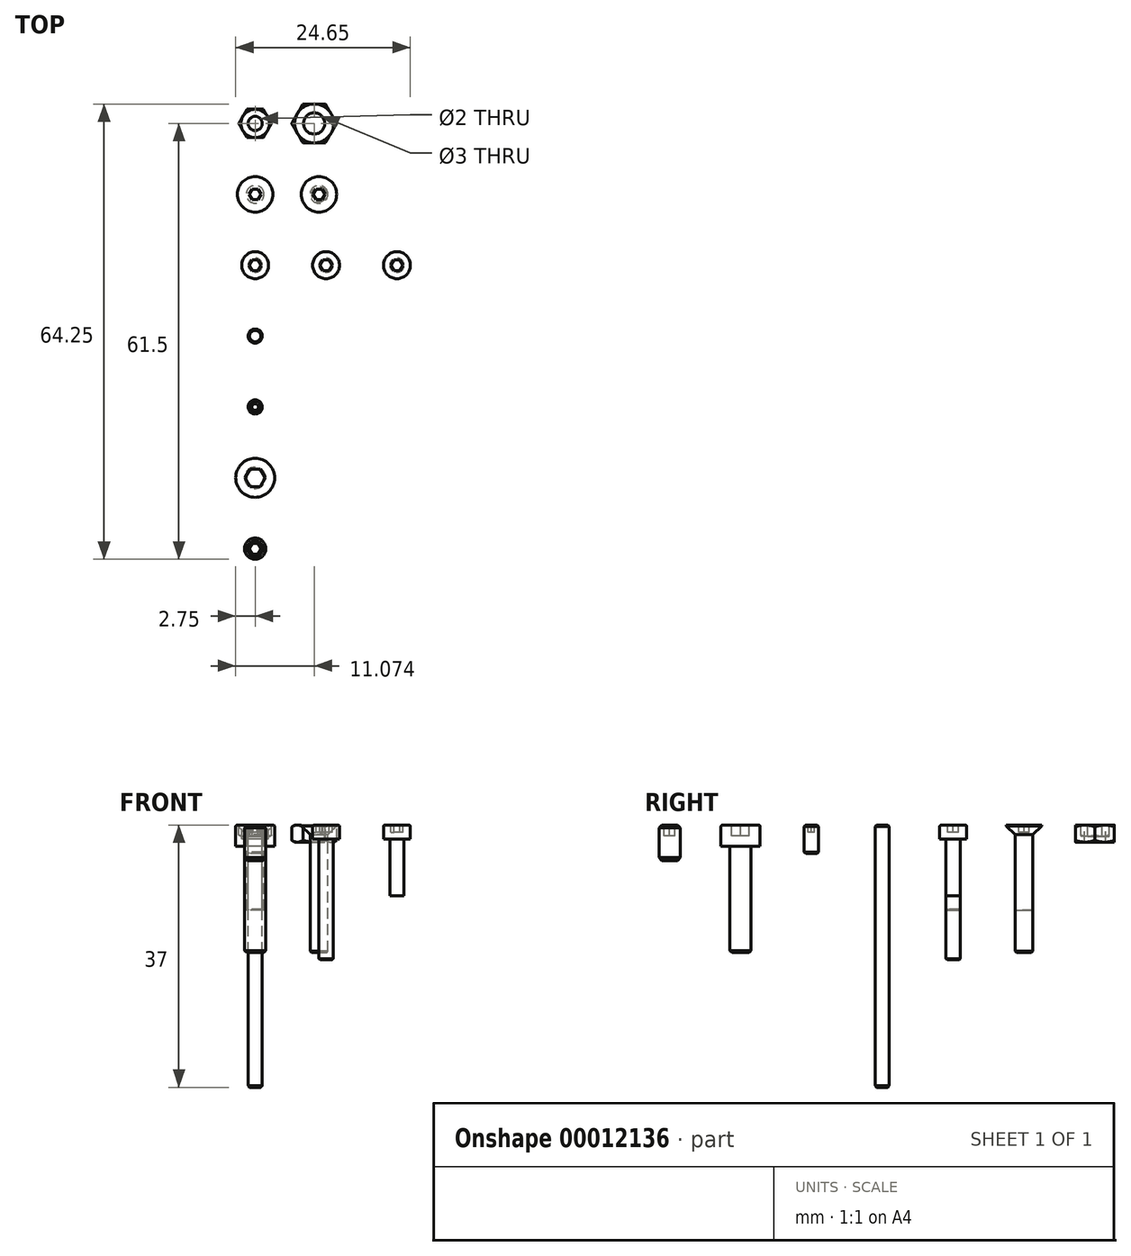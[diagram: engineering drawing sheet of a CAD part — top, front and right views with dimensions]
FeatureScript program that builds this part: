
annotation { "Feature Type Name" : "Feature", "Feature Type Description" : "" }
export const myFeature = defineFeature(function(context is Context, id is Id, definition is map)
    precondition{}
    {
        {
            var Q0;
            Q0=qCreatedBy(makeId("Top.planeOp"),FACE);
            var sketch = newSketch(context, id + "F0", { "sketchPlane" : qUnion([Q0])});
            skCircle(sketch, "E0.cCircle", {"center": v(0, 0) * mm, "radius": 2 * mm, "construction": true});
            skLineSegment(sketch, "E0.0", {"start": v(1.15, -2) * mm, "end": v(-1.15, -2) * mm});
            skLineSegment(sketch, "E0.1", {"start": v(-1.15, -2) * mm, "end": v(-2.3, 0) * mm});
            skLineSegment(sketch, "E0.2", {"start": v(-2.3, 0) * mm, "end": v(-1.15, 2) * mm});
            skLineSegment(sketch, "E0.3", {"start": v(-1.15, 2) * mm, "end": v(1.15, 2) * mm});
            skLineSegment(sketch, "E0.4", {"start": v(1.15, 2) * mm, "end": v(2.3, 0) * mm});
            skLineSegment(sketch, "E0.5", {"start": v(2.3, 0) * mm, "end": v(1.15, -2) * mm});
            skPoint(sketch, "E0.0.midPoint", {"position": v(0, -2) * mm});
            skCircle(sketch, "E1", {"center": v(0, 0) * mm, "radius": 1 * mm});
            skCircle(sketch, "E2", {"center": v(0, 0) * mm, "radius": 2 * mm});
            skSolve(sketch);
        }
        {
            var Q0;
            {var subQ1=sQuery(id+"F0.wireOp",EDGE,"E0.3");var subQ3=sQuery(id+"F0.wireOp",EDGE,"E0.2");var subQ5=makeQuery(id+"F0.imprint","INTERSECT",VERTEX,{"derivedFrom":[subQ3,subQ1]});Q0=makeQuery(id+"F0.imprint","IMPRINT",FACE,{"disambiguationData":[TD([[makeQuery(id+"F0.imprint","IMPRINT",EDGE,{"disambiguationData":[TD([[subQ5,1.0]])],"derivedFrom":subQ3}),-1.0]])]});}
            var Q1;
            {var subQ1=sQuery(id+"F0.wireOp",EDGE,"E0.2");var subQ3=sQuery(id+"F0.wireOp",EDGE,"E0.1");var subQ5=makeQuery(id+"F0.imprint","INTERSECT",VERTEX,{"derivedFrom":[subQ3,subQ1]});Q1=makeQuery(id+"F0.imprint","IMPRINT",FACE,{"disambiguationData":[TD([[makeQuery(id+"F0.imprint","IMPRINT",EDGE,{"disambiguationData":[TD([[subQ5,1.0]])],"derivedFrom":subQ3}),-1.0]])]});}
            var Q2;
            Q2=makeQuery(id+"F0.imprint","IMPRINT",FACE,{"disambiguationData":[TD([[makeQuery(id+"F0.imprint","IMPRINT",EDGE,{"derivedFrom":sQuery(id+"F0.wireOp",EDGE,"E1")}),-1.0]])]});
            var Q3;
            {var subQ1=sQuery(id+"F0.wireOp",EDGE,"E0.4");var subQ3=sQuery(id+"F0.wireOp",EDGE,"E0.3");var subQ5=makeQuery(id+"F0.imprint","INTERSECT",VERTEX,{"derivedFrom":[subQ3,subQ1]});Q3=makeQuery(id+"F0.imprint","IMPRINT",FACE,{"disambiguationData":[TD([[makeQuery(id+"F0.imprint","IMPRINT",EDGE,{"disambiguationData":[TD([[subQ5,1.0]])],"derivedFrom":subQ3}),-1.0]])]});}
            var Q4;
            {var subQ1=sQuery(id+"F0.wireOp",EDGE,"E0.5");var subQ3=sQuery(id+"F0.wireOp",EDGE,"E0.4");var subQ5=makeQuery(id+"F0.imprint","INTERSECT",VERTEX,{"derivedFrom":[subQ3,subQ1]});Q4=makeQuery(id+"F0.imprint","IMPRINT",FACE,{"disambiguationData":[TD([[makeQuery(id+"F0.imprint","IMPRINT",EDGE,{"disambiguationData":[TD([[subQ5,1.0]])],"derivedFrom":subQ3}),-1.0]])]});}
            var Q5;
            {var subQ1=sQuery(id+"F0.wireOp",EDGE,"E0.5");var subQ3=sQuery(id+"F0.wireOp",EDGE,"E0.0");var subQ5=makeQuery(id+"F0.imprint","INTERSECT",VERTEX,{"derivedFrom":[subQ3,subQ1]});Q5=makeQuery(id+"F0.imprint","IMPRINT",FACE,{"disambiguationData":[TD([[makeQuery(id+"F0.imprint","IMPRINT",EDGE,{"disambiguationData":[TD([[subQ5,-1.0]])],"derivedFrom":subQ3}),-1.0]])]});}
            var Q6;
            {var subQ1=sQuery(id+"F0.wireOp",EDGE,"E0.1");var subQ3=sQuery(id+"F0.wireOp",EDGE,"E0.0");var subQ5=makeQuery(id+"F0.imprint","INTERSECT",VERTEX,{"derivedFrom":[subQ3,subQ1]});Q6=makeQuery(id+"F0.imprint","IMPRINT",FACE,{"disambiguationData":[TD([[makeQuery(id+"F0.imprint","IMPRINT",EDGE,{"disambiguationData":[TD([[subQ5,1.0]])],"derivedFrom":subQ3}),-1.0]])]});}
            extrude(context, id + "F1", {"entities" : qUnion([Q0, Q1, Q2, Q3, Q4, Q5, Q6]), "oppositeDirection" : true, "depth" : 1.6 * mm});
        }
        {
            var Q0;
            Q0=qCreatedBy(makeId("Front.planeOp"),FACE);
            var sketch = newSketch(context, id + "F2", { "sketchPlane" : qUnion([Q0])});
            skLineSegment(sketch, "E3.0", {"start": v(-2, 0) * mm, "end": v(2, 0) * mm});
            skLineSegment(sketch, "E3.1", {"start": v(2.3, -1.6) * mm, "end": v(2.3, 0) * mm});
            skLineSegment(sketch, "E3.2", {"start": v(-2.3, -1.6) * mm, "end": v(-2.3, 0) * mm});
            skLineSegment(sketch, "E4", {"start": v(2, 0) * mm, "end": v(2.3, -0.18) * mm});
            skLineSegment(sketch, "E5", {"start": v(2, 0) * mm, "end": v(2.3, 0) * mm});
            skLineSegment(sketch, "E6", {"start": v(0, 0) * mm, "end": v(0, -1.88) * mm, "construction": true});
            skLineSegment(sketch, "E7", {"start": v(-2.3, -0.8) * mm, "end": v(0, -0.8) * mm, "construction": true});
            skLineSegment(sketch, "E8.0.MirrorCS", {"start": v(2, -1.6) * mm, "end": v(2.3, -1.6) * mm});
            skLineSegment(sketch, "E9.0.MirrorCS", {"start": v(2.3, 0) * mm, "end": v(2.3, -1.6) * mm});
            skLineSegment(sketch, "E10.0.MirrorCS", {"start": v(2, -1.6) * mm, "end": v(2.3, -1.42) * mm});
            skSolve(sketch);
        }
        {
            var Q0;
            {var subQ2=sQuery(id+"F2.wireOp",EDGE,"E4");Q0=makeQuery(id+"F2.imprint","IMPRINT",FACE,{"disambiguationData":[TD([[makeQuery(id+"F2.imprint","IMPRINT",EDGE,{"derivedFrom":subQ2}),1.0]])]});}
            var Q1;
            {var subQ2=sQuery(id+"F2.wireOp",EDGE,"E8.0.MirrorCS");Q1=makeQuery(id+"F2.imprint","IMPRINT",FACE,{"disambiguationData":[TD([[makeQuery(id+"F2.imprint","IMPRINT",EDGE,{"derivedFrom":subQ2}),1.0]])]});}
            var Q2;
            Q2=sQuery(id+"F2.wireOp",EDGE,"E6");
            revolve(context, id + "F3", {"operationType" : NewBodyOperationType.REMOVE, "entities" : qUnion([Q0, Q1]), "axis" : qUnion([Q2]), "revolveType" : RevolveType.FULL, "oppositeDirection" : true});
        }
        {
            var Q0;
            Q0=qCreatedBy(makeId("Top.planeOp"),FACE);
            var sketch = newSketch(context, id + "F4", { "sketchPlane" : qUnion([Q0])});
            skCircle(sketch, "E11.cCircle", {"center": v(8.32, 0) * mm, "radius": 2.75 * mm, "construction": true});
            skLineSegment(sketch, "E11.0", {"start": v(9.91, -2.75) * mm, "end": v(6.74, -2.75) * mm});
            skLineSegment(sketch, "E11.1", {"start": v(6.74, -2.75) * mm, "end": v(5.15, 0) * mm});
            skLineSegment(sketch, "E11.2", {"start": v(5.15, 0) * mm, "end": v(6.74, 2.75) * mm});
            skLineSegment(sketch, "E11.3", {"start": v(6.74, 2.75) * mm, "end": v(9.91, 2.75) * mm});
            skLineSegment(sketch, "E11.4", {"start": v(9.91, 2.75) * mm, "end": v(11.5, 0) * mm});
            skLineSegment(sketch, "E11.5", {"start": v(11.5, 0) * mm, "end": v(9.91, -2.75) * mm});
            skPoint(sketch, "E11.0.midPoint", {"position": v(8.32, -2.75) * mm});
            skCircle(sketch, "E12", {"center": v(8.32, 0) * mm, "radius": 1.5 * mm});
            skSolve(sketch);
        }
        {
            var Q0;
            Q0=makeQuery(id+"F4.imprint","IMPRINT",FACE,{"disambiguationData":[TD([[makeQuery(id+"F4.imprint","IMPRINT",EDGE,{"derivedFrom":sQuery(id+"F4.wireOp",EDGE,"E11.0")}),-1.0]])]});
            extrude(context, id + "F5", {"entities" : qUnion([Q0]), "oppositeDirection" : true, "depth" : 2.4 * mm});
        }
        {
            var Q0;
            Q0=qCreatedBy(makeId("Front.planeOp"),FACE);
            var sketch = newSketch(context, id + "F6", { "sketchPlane" : qUnion([Q0])});
            skLineSegment(sketch, "E13.0", {"start": v(5.57, 0) * mm, "end": v(11.07, 0) * mm});
            skLineSegment(sketch, "E13.1", {"start": v(5.15, -2.4) * mm, "end": v(5.15, 0) * mm});
            skLineSegment(sketch, "E13.2", {"start": v(11.5, -2.4) * mm, "end": v(11.5, 0) * mm});
            skLineSegment(sketch, "E14", {"start": v(5.57, 0) * mm, "end": v(5.15, -0.25) * mm});
            skLineSegment(sketch, "E15", {"start": v(5.57, 0) * mm, "end": v(5.15, 0) * mm});
            skLineSegment(sketch, "E16", {"start": v(8.32, 0) * mm, "end": v(8.32, -2.47) * mm, "construction": true});
            skLineSegment(sketch, "E17", {"start": v(11.5, -1.2) * mm, "end": v(8.32, -1.2) * mm, "construction": true});
            skLineSegment(sketch, "E18.0.MirrorCS", {"start": v(5.57, -2.4) * mm, "end": v(5.15, -2.15) * mm});
            skLineSegment(sketch, "E19.0.MirrorCS", {"start": v(5.15, 0) * mm, "end": v(5.15, -2.4) * mm});
            skLineSegment(sketch, "E20.0.MirrorCS", {"start": v(5.57, -2.4) * mm, "end": v(5.15, -2.4) * mm});
            skSolve(sketch);
        }
        {
            var Q0;
            {var subQ2=sQuery(id+"F6.wireOp",EDGE,"E14");Q0=makeQuery(id+"F6.imprint","IMPRINT",FACE,{"disambiguationData":[TD([[makeQuery(id+"F6.imprint","IMPRINT",EDGE,{"derivedFrom":subQ2}),-1.0]])]});}
            var Q1;
            {var subQ2=sQuery(id+"F6.wireOp",EDGE,"E18.0.MirrorCS");Q1=makeQuery(id+"F6.imprint","IMPRINT",FACE,{"disambiguationData":[TD([[makeQuery(id+"F6.imprint","IMPRINT",EDGE,{"derivedFrom":subQ2}),1.0]])]});}
            var Q2;
            Q2=sQuery(id+"F6.wireOp",EDGE,"E16");
            revolve(context, id + "F7", {"operationType" : NewBodyOperationType.REMOVE, "entities" : qUnion([Q0, Q1]), "axis" : qUnion([Q2]), "revolveType" : RevolveType.FULL, "oppositeDirection" : true});
        }
        {
            var Q0;
            Q0=qCreatedBy(makeId("Top.planeOp"),FACE);
            var sketch = newSketch(context, id + "F8", { "sketchPlane" : qUnion([Q0])});
            skCircle(sketch, "E21", {"center": v(17, 0) * mm, "radius": 2.5 * mm});
            skCircle(sketch, "E22", {"center": v(17, 0) * mm, "radius": 1.25 * mm});
            skCircle(sketch, "E23.cCircle", {"center": v(17, 0) * mm, "radius": 0.75 * mm, "construction": true});
            skLineSegment(sketch, "E23.0", {"start": v(17.43, -0.75) * mm, "end": v(16.57, -0.75) * mm});
            skLineSegment(sketch, "E23.1", {"start": v(16.57, -0.75) * mm, "end": v(16.13, 0) * mm});
            skLineSegment(sketch, "E23.2", {"start": v(16.13, 0) * mm, "end": v(16.57, 0.75) * mm});
            skLineSegment(sketch, "E23.3", {"start": v(16.57, 0.75) * mm, "end": v(17.43, 0.75) * mm});
            skLineSegment(sketch, "E23.4", {"start": v(17.43, 0.75) * mm, "end": v(17.87, 0) * mm});
            skLineSegment(sketch, "E23.5", {"start": v(17.87, 0) * mm, "end": v(17.43, -0.75) * mm});
            skPoint(sketch, "E23.0.midPoint", {"position": v(17, -0.75) * mm});
            skSolve(sketch);
        }
        {
            var Q0;
            Q0=makeQuery(id+"F8.imprint","IMPRINT",FACE,{"disambiguationData":[TD([[makeQuery(id+"F8.imprint","IMPRINT",EDGE,{"derivedFrom":sQuery(id+"F8.wireOp",EDGE,"E22")}),1.0]])]});
            var Q1;
            Q1=makeQuery(id+"F8.imprint","IMPRINT",FACE,{"disambiguationData":[TD([[makeQuery(id+"F8.imprint","IMPRINT",EDGE,{"derivedFrom":sQuery(id+"F8.wireOp",EDGE,"E23.0")}),-1.0]])]});
            extrude(context, id + "F9", {"entities" : qUnion([Q0, Q1]), "oppositeDirection" : true, "depth" : 15 * mm});
        }
        {
            var Q0;
            Q0=makeQuery(id+"F8.imprint","IMPRINT",FACE,{"disambiguationData":[TD([[makeQuery(id+"F8.imprint","IMPRINT",EDGE,{"derivedFrom":sQuery(id+"F8.wireOp",EDGE,"E21")}),1.0]])]});
            extrude(context, id + "F10", {"entities" : qUnion([Q0]), "operationType" : NewBodyOperationType.ADD, "oppositeDirection" : true, "depth" : 1.5 * mm});
        }
        {
            var Q0;
            Q0=makeQuery(id+"F10.opExtrude","CAP_EDGE",EDGE,{"disambiguationData":[OSD([sQuery(id+"F8.wireOp",EDGE,"E21")])],"isStart":false});
            chamfer(context, id + "F11", {"entities" : qUnion([Q0]), "width" : 1.4 * mm, "tangentPropagation" : true});
        }
        {
            var Q0;
            Q0=makeQuery(id+"F8.imprint","IMPRINT",FACE,{"disambiguationData":[TD([[makeQuery(id+"F8.imprint","IMPRINT",EDGE,{"derivedFrom":sQuery(id+"F8.wireOp",EDGE,"E23.0")}),-1.0]])]});
            extrude(context, id + "F12", {"entities" : qUnion([Q0]), "operationType" : NewBodyOperationType.REMOVE, "oppositeDirection" : true, "depth" : 1 * mm});
        }
        {
            var Q0;
            Q0=makeQuery(id+"F9.opExtrude","SWEPT_BODY",BODY,{"disambiguationData":[OSD([sQuery(id+"F8.wireOp",EDGE,"E22")])]});
            transform(context, id + "F13", {"entities" : qUnion([Q0]), "transformType" : TransformType.TRANSLATION_3D, "dx" : 10 * mm, "dy" : 0 * mm, "dz" : 0 * mm, "makeCopy" : true});
        }
        {
            var Q0;
            Q0=makeQuery(id+"F13.opPattern","COPY",FACE,{"derivedFrom":makeQuery(id+"F9.opExtrude","CAP_FACE",FACE,{"disambiguationData":[OSD([sQuery(id+"F8.wireOp",EDGE,"E22")])],"isStart":false}),"instanceName":"1"});
            extrude(context, id + "F14", {"entities" : qUnion([Q0]), "operationType" : NewBodyOperationType.ADD, "depth" : 3 * mm});
        }
        {
            var Q0;
            Q0=makeQuery(id+"F9.opExtrude","SWEPT_BODY",BODY,{"disambiguationData":[OSD([sQuery(id+"F8.wireOp",EDGE,"E22")])]});
            transform(context, id + "F15", {"entities" : qUnion([Q0]), "transformType" : TransformType.TRANSLATION_3D, "dx" : -17 * mm, "dy" : -10 * mm, "dz" : 0 * mm, "makeCopy" : false});
        }
        {
            var Q0;
            Q0=makeQuery(id+"F13.opPattern","COPY",BODY,{"derivedFrom":makeQuery(id+"F9.opExtrude","SWEPT_BODY",BODY,{"disambiguationData":[OSD([sQuery(id+"F8.wireOp",EDGE,"E22")])]}),"instanceName":"1"});
            transform(context, id + "F16", {"entities" : qUnion([Q0]), "transformType" : TransformType.TRANSLATION_3D, "dx" : -18 * mm, "dy" : -10 * mm, "dz" : 0 * mm, "makeCopy" : false});
        }
        {
            var Q0;
            Q0=qCreatedBy(makeId("Top.planeOp"),FACE);
            var sketch = newSketch(context, id + "F17", { "sketchPlane" : qUnion([Q0])});
            skCircle(sketch, "E24", {"center": v(0, -20) * mm, "radius": 1.9 * mm});
            skCircle(sketch, "E25", {"center": v(0, -20) * mm, "radius": 1 * mm});
            skCircle(sketch, "E26.cCircle", {"center": v(0, -20) * mm, "radius": 0.75 * mm, "construction": true});
            skLineSegment(sketch, "E26.0", {"start": v(0.43, -20.75) * mm, "end": v(-0.43, -20.75) * mm});
            skLineSegment(sketch, "E26.1", {"start": v(-0.43, -20.75) * mm, "end": v(-0.87, -20) * mm});
            skLineSegment(sketch, "E26.2", {"start": v(-0.87, -20) * mm, "end": v(-0.43, -19.25) * mm});
            skLineSegment(sketch, "E26.3", {"start": v(-0.43, -19.25) * mm, "end": v(0.43, -19.25) * mm});
            skLineSegment(sketch, "E26.4", {"start": v(0.43, -19.25) * mm, "end": v(0.87, -20) * mm});
            skLineSegment(sketch, "E26.5", {"start": v(0.87, -20) * mm, "end": v(0.43, -20.75) * mm});
            skPoint(sketch, "E26.0.midPoint", {"position": v(0, -20.75) * mm});
            skSolve(sketch);
        }
        {
            var Q0;
            Q0=makeQuery(id+"F17.imprint","IMPRINT",FACE,{"disambiguationData":[TD([[makeQuery(id+"F17.imprint","IMPRINT",EDGE,{"derivedFrom":sQuery(id+"F17.wireOp",EDGE,"E25")}),1.0]])]});
            var Q1;
            Q1=makeQuery(id+"F17.imprint","IMPRINT",FACE,{"disambiguationData":[TD([[makeQuery(id+"F17.imprint","IMPRINT",EDGE,{"derivedFrom":sQuery(id+"F17.wireOp",EDGE,"E26.0")}),-1.0]])]});
            extrude(context, id + "F18", {"entities" : qUnion([Q0, Q1]), "oppositeDirection" : true, "depth" : 12 * mm});
        }
        {
            var Q0;
            Q0=makeQuery(id+"F17.imprint","IMPRINT",FACE,{"disambiguationData":[TD([[makeQuery(id+"F17.imprint","IMPRINT",EDGE,{"derivedFrom":sQuery(id+"F17.wireOp",EDGE,"E24")}),1.0]])]});
            extrude(context, id + "F19", {"entities" : qUnion([Q0]), "operationType" : NewBodyOperationType.ADD, "oppositeDirection" : true, "depth" : 2 * mm});
        }
        {
            var Q0;
            Q0=makeQuery(id+"F17.imprint","IMPRINT",FACE,{"disambiguationData":[TD([[makeQuery(id+"F17.imprint","IMPRINT",EDGE,{"derivedFrom":sQuery(id+"F17.wireOp",EDGE,"E26.0")}),-1.0]])]});
            extrude(context, id + "F20", {"entities" : qUnion([Q0]), "operationType" : NewBodyOperationType.REMOVE, "oppositeDirection" : true, "depth" : 1 * mm});
        }
        {
            var Q0;
            Q0=makeQuery(id+"F19.opExtrude","CAP_EDGE",EDGE,{"disambiguationData":[OSD([sQuery(id+"F17.wireOp",EDGE,"E24")])],"isStart":true});
            fillet(context, id + "F21", {"entities" : qUnion([Q0]), "radius" : 0.2 * mm, "tangentPropagation" : true, "allowEdgeOverflow" : false});
        }
        {
            var Q0;
            Q0=makeQuery(id+"F18.opExtrude","SWEPT_BODY",BODY,{"disambiguationData":[OSD([sQuery(id+"F17.wireOp",EDGE,"E25")])]});
            transform(context, id + "F22", {"entities" : qUnion([Q0]), "transformType" : TransformType.TRANSLATION_3D, "dx" : 10 * mm, "dy" : 0 * mm, "dz" : 0 * mm, "makeCopy" : true});
        }
        {
            var Q0;
            Q0=makeQuery(id+"F22.opPattern","COPY",FACE,{"derivedFrom":makeQuery(id+"F18.opExtrude","CAP_FACE",FACE,{"disambiguationData":[OSD([sQuery(id+"F17.wireOp",EDGE,"E25")])],"isStart":false}),"instanceName":"1"});
            extrude(context, id + "F23", {"entities" : qUnion([Q0]), "operationType" : NewBodyOperationType.ADD, "depth" : 7 * mm});
        }
        {
            var Q0;
            Q0=qCreatedBy(makeId("Top.planeOp"),FACE);
            var sketch = newSketch(context, id + "F24", { "sketchPlane" : qUnion([Q0])});
            skCircle(sketch, "E27", {"center": v(0, -30) * mm, "radius": 1 * mm});
            skSolve(sketch);
        }
        {
            var Q0;
            Q0=makeQuery(id+"F24.imprint","IMPRINT",FACE,{"disambiguationData":[TD([[makeQuery(id+"F24.imprint","IMPRINT",EDGE,{"derivedFrom":sQuery(id+"F24.wireOp",EDGE,"E27")}),1.0]])]});
            extrude(context, id + "F25", {"entities" : qUnion([Q0]), "oppositeDirection" : true, "depth" : 37 * mm});
        }
        {
            var Q0;
            Q0=makeQuery(id+"F25.opExtrude","CAP_EDGE",EDGE,{"disambiguationData":[OSD([sQuery(id+"F24.wireOp",EDGE,"E27")])],"isStart":false});
            var Q1;
            Q1=makeQuery(id+"F25.opExtrude","CAP_EDGE",EDGE,{"disambiguationData":[OSD([sQuery(id+"F24.wireOp",EDGE,"E27")])],"isStart":true});
            chamfer(context, id + "F26", {"entities" : qUnion([Q0, Q1]), "width" : 0.2 * mm, "tangentPropagation" : true});
        }
        {
            var Q0;
            Q0=makeQuery(id+"F22.opPattern","COPY",BODY,{"derivedFrom":makeQuery(id+"F18.opExtrude","SWEPT_BODY",BODY,{"disambiguationData":[OSD([sQuery(id+"F17.wireOp",EDGE,"E25")])]}),"instanceName":"1"});
            transform(context, id + "F27", {"entities" : qUnion([Q0]), "transformType" : TransformType.TRANSLATION_3D, "dx" : 10 * mm, "dy" : 0 * mm, "dz" : 0 * mm, "makeCopy" : true});
        }
        {
            var Q0;
            Q0=makeQuery(id+"F27.opPattern","COPY",FACE,{"derivedFrom":makeQuery(id+"F23.opExtrude","CAP_FACE",FACE,{"disambiguationData":[OSD([sQuery(id+"F17.wireOp",EDGE,"E25")])],"isStart":false}),"instanceName":"1"});
            extrude(context, id + "F28", {"entities" : qUnion([Q0]), "operationType" : NewBodyOperationType.REMOVE, "oppositeDirection" : true, "depth" : 9 * mm});
        }
        {
            var Q0;
            Q0=qCreatedBy(makeId("Top.planeOp"),FACE);
            var sketch = newSketch(context, id + "F29", { "sketchPlane" : qUnion([Q0])});
            skCircle(sketch, "E28", {"center": v(0, -40) * mm, "radius": 1 * mm});
            skCircle(sketch, "E29.cCircle", {"center": v(0, -40) * mm, "radius": 0.45 * mm, "construction": true});
            skLineSegment(sketch, "E29.0", {"start": v(0.26, -40.45) * mm, "end": v(-0.26, -40.45) * mm});
            skLineSegment(sketch, "E29.1", {"start": v(-0.26, -40.45) * mm, "end": v(-0.52, -40) * mm});
            skLineSegment(sketch, "E29.2", {"start": v(-0.52, -40) * mm, "end": v(-0.26, -39.55) * mm});
            skLineSegment(sketch, "E29.3", {"start": v(-0.26, -39.55) * mm, "end": v(0.26, -39.55) * mm});
            skLineSegment(sketch, "E29.4", {"start": v(0.26, -39.55) * mm, "end": v(0.52, -40) * mm});
            skLineSegment(sketch, "E29.5", {"start": v(0.52, -40) * mm, "end": v(0.26, -40.45) * mm});
            skPoint(sketch, "E29.0.midPoint", {"position": v(0, -40.45) * mm});
            skSolve(sketch);
        }
        {
            var Q0;
            Q0=makeQuery(id+"F29.imprint","IMPRINT",FACE,{"disambiguationData":[TD([[makeQuery(id+"F29.imprint","IMPRINT",EDGE,{"derivedFrom":sQuery(id+"F29.wireOp",EDGE,"E28")}),1.0]])]});
            var Q1;
            Q1=makeQuery(id+"F29.imprint","IMPRINT",FACE,{"disambiguationData":[TD([[makeQuery(id+"F29.imprint","IMPRINT",EDGE,{"derivedFrom":sQuery(id+"F29.wireOp",EDGE,"E29.0")}),-1.0]])]});
            extrude(context, id + "F30", {"entities" : qUnion([Q0, Q1]), "oppositeDirection" : true, "depth" : 4 * mm});
        }
        {
            var Q0;
            Q0=makeQuery(id+"F29.imprint","IMPRINT",FACE,{"disambiguationData":[TD([[makeQuery(id+"F29.imprint","IMPRINT",EDGE,{"derivedFrom":sQuery(id+"F29.wireOp",EDGE,"E29.0")}),-1.0]])]});
            extrude(context, id + "F31", {"entities" : qUnion([Q0]), "operationType" : NewBodyOperationType.REMOVE, "oppositeDirection" : true, "depth" : 1 * mm});
        }
        {
            var Q0;
            Q0=makeQuery(id+"F30.opExtrude","CAP_EDGE",EDGE,{"disambiguationData":[OSD([sQuery(id+"F29.wireOp",EDGE,"E28")])],"isStart":true});
            var Q1;
            Q1=makeQuery(id+"F30.opExtrude","CAP_EDGE",EDGE,{"disambiguationData":[OSD([sQuery(id+"F29.wireOp",EDGE,"E28")])],"isStart":false});
            chamfer(context, id + "F32", {"entities" : qUnion([Q0, Q1]), "width" : 0.2 * mm, "tangentPropagation" : true});
        }
        {
            var Q0;
            Q0=qCreatedBy(makeId("Top.planeOp"),FACE);
            var sketch = newSketch(context, id + "F33", { "sketchPlane" : qUnion([Q0])});
            skCircle(sketch, "E30", {"center": v(0, -50) * mm, "radius": 1.5 * mm});
            skCircle(sketch, "E31", {"center": v(0, -50) * mm, "radius": 2.75 * mm});
            skCircle(sketch, "E32.cCircle", {"center": v(0, -50) * mm, "radius": 1.25 * mm, "construction": true});
            skLineSegment(sketch, "E32.0", {"start": v(0.72, -51.25) * mm, "end": v(-0.72, -51.25) * mm});
            skLineSegment(sketch, "E32.1", {"start": v(-0.72, -51.25) * mm, "end": v(-1.44, -50) * mm});
            skLineSegment(sketch, "E32.2", {"start": v(-1.44, -50) * mm, "end": v(-0.72, -48.75) * mm});
            skLineSegment(sketch, "E32.3", {"start": v(-0.72, -48.75) * mm, "end": v(0.72, -48.75) * mm});
            skLineSegment(sketch, "E32.4", {"start": v(0.72, -48.75) * mm, "end": v(1.44, -50) * mm});
            skLineSegment(sketch, "E32.5", {"start": v(1.44, -50) * mm, "end": v(0.72, -51.25) * mm});
            skPoint(sketch, "E32.0.midPoint", {"position": v(0, -51.25) * mm});
            skSolve(sketch);
        }
        {
            var Q0;
            Q0=makeQuery(id+"F33.imprint","IMPRINT",FACE,{"disambiguationData":[TD([[makeQuery(id+"F33.imprint","IMPRINT",EDGE,{"derivedFrom":sQuery(id+"F33.wireOp",EDGE,"E32.0")}),-1.0]])]});
            var Q1;
            Q1=makeQuery(id+"F33.imprint","IMPRINT",FACE,{"disambiguationData":[TD([[makeQuery(id+"F33.imprint","IMPRINT",EDGE,{"derivedFrom":sQuery(id+"F33.wireOp",EDGE,"E30")}),1.0]])]});
            extrude(context, id + "F34", {"entities" : qUnion([Q0, Q1]), "oppositeDirection" : true, "depth" : 18 * mm});
        }
        {
            var Q0;
            Q0=makeQuery(id+"F33.imprint","IMPRINT",FACE,{"disambiguationData":[TD([[makeQuery(id+"F33.imprint","IMPRINT",EDGE,{"derivedFrom":sQuery(id+"F33.wireOp",EDGE,"E30")}),-1.0]])]});
            extrude(context, id + "F35", {"entities" : qUnion([Q0]), "operationType" : NewBodyOperationType.ADD, "oppositeDirection" : true, "depth" : 3 * mm});
        }
        {
            var Q0;
            Q0=makeQuery(id+"F33.imprint","IMPRINT",FACE,{"disambiguationData":[TD([[makeQuery(id+"F33.imprint","IMPRINT",EDGE,{"derivedFrom":sQuery(id+"F33.wireOp",EDGE,"E32.0")}),-1.0]])]});
            extrude(context, id + "F36", {"entities" : qUnion([Q0]), "operationType" : NewBodyOperationType.REMOVE, "oppositeDirection" : true, "depth" : 1.5 * mm});
        }
        {
            var Q0;
            Q0=makeQuery(id+"F35.opExtrude","CAP_EDGE",EDGE,{"disambiguationData":[OSD([sQuery(id+"F33.wireOp",EDGE,"E31")])],"isStart":true});
            fillet(context, id + "F37", {"entities" : qUnion([Q0]), "radius" : 0.2 * mm, "tangentPropagation" : true, "allowEdgeOverflow" : false});
        }
        {
            var Q0;
            Q0=qCreatedBy(makeId("Top.planeOp"),FACE);
            var sketch = newSketch(context, id + "F38", { "sketchPlane" : qUnion([Q0])});
            skCircle(sketch, "E33", {"center": v(0, -60) * mm, "radius": 1.5 * mm});
            skCircle(sketch, "E34.cCircle", {"center": v(0, -60) * mm, "radius": 0.75 * mm, "construction": true});
            skLineSegment(sketch, "E34.0", {"start": v(0.43, -60.75) * mm, "end": v(-0.43, -60.75) * mm});
            skLineSegment(sketch, "E34.1", {"start": v(-0.43, -60.75) * mm, "end": v(-0.87, -60) * mm});
            skLineSegment(sketch, "E34.2", {"start": v(-0.87, -60) * mm, "end": v(-0.43, -59.25) * mm});
            skLineSegment(sketch, "E34.3", {"start": v(-0.43, -59.25) * mm, "end": v(0.43, -59.25) * mm});
            skLineSegment(sketch, "E34.4", {"start": v(0.43, -59.25) * mm, "end": v(0.87, -60) * mm});
            skLineSegment(sketch, "E34.5", {"start": v(0.87, -60) * mm, "end": v(0.43, -60.75) * mm});
            skPoint(sketch, "E34.0.midPoint", {"position": v(0, -60.75) * mm});
            skSolve(sketch);
        }
        {
            var Q0;
            Q0=makeQuery(id+"F38.imprint","IMPRINT",FACE,{"disambiguationData":[TD([[makeQuery(id+"F38.imprint","IMPRINT",EDGE,{"derivedFrom":sQuery(id+"F38.wireOp",EDGE,"E33")}),1.0]])]});
            var Q1;
            Q1=makeQuery(id+"F38.imprint","IMPRINT",FACE,{"disambiguationData":[TD([[makeQuery(id+"F38.imprint","IMPRINT",EDGE,{"derivedFrom":sQuery(id+"F38.wireOp",EDGE,"E34.0")}),-1.0]])]});
            extrude(context, id + "F39", {"entities" : qUnion([Q0, Q1]), "oppositeDirection" : true, "depth" : 5 * mm});
        }
        {
            var Q0;
            Q0=makeQuery(id+"F38.imprint","IMPRINT",FACE,{"disambiguationData":[TD([[makeQuery(id+"F38.imprint","IMPRINT",EDGE,{"derivedFrom":sQuery(id+"F38.wireOp",EDGE,"E34.0")}),-1.0]])]});
            extrude(context, id + "F40", {"entities" : qUnion([Q0]), "operationType" : NewBodyOperationType.REMOVE, "oppositeDirection" : true, "depth" : 1.5 * mm});
        }
        {
            var Q0;
            Q0=makeQuery(id+"F39.opExtrude","CAP_EDGE",EDGE,{"disambiguationData":[OSD([sQuery(id+"F38.wireOp",EDGE,"E33")])],"isStart":true});
            var Q1;
            Q1=makeQuery(id+"F39.opExtrude","CAP_EDGE",EDGE,{"disambiguationData":[OSD([sQuery(id+"F38.wireOp",EDGE,"E33")])],"isStart":false});
            chamfer(context, id + "F41", {"entities" : qUnion([Q0, Q1]), "width" : 0.4 * mm, "tangentPropagation" : true});
        }
        {
            var Q0;
            Q0=makeQuery(id+"F9.opExtrude","CAP_FACE",FACE,{"disambiguationData":[OSD([sQuery(id+"F8.wireOp",EDGE,"E22")])],"isStart":false});
            extrude(context, id + "F42", {"entities" : qUnion([Q0]), "operationType" : NewBodyOperationType.REMOVE, "oppositeDirection" : true, "depth" : 3 * mm});
        }
        {
            var Q0;
            Q0=makeQuery(id+"F18.opExtrude","CAP_EDGE",EDGE,{"disambiguationData":[OSD([sQuery(id+"F17.wireOp",EDGE,"E25")])],"isStart":false});
            var Q1;
            Q1=makeQuery(id+"F23.opExtrude","CAP_EDGE",EDGE,{"disambiguationData":[OSD([sQuery(id+"F17.wireOp",EDGE,"E25")])],"isStart":false});
            var Q2;
            Q2=makeQuery(id+"F28.boolean.opBoolean","COPY",EDGE,{"derivedFrom":makeQuery(id+"F28.opExtrude","CAP_EDGE",EDGE,{"disambiguationData":[OSD([sQuery(id+"F17.wireOp",EDGE,"E25")])],"isStart":false})});
            chamfer(context, id + "F43", {"entities" : qUnion([Q0, Q1, Q2]), "width" : 0.15 * mm, "tangentPropagation" : true});
        }
        {
            var Q0;
            Q0=makeQuery(id+"F42.boolean.opBoolean","COPY",EDGE,{"derivedFrom":makeQuery(id+"F42.opExtrude","CAP_EDGE",EDGE,{"disambiguationData":[OSD([sQuery(id+"F8.wireOp",EDGE,"E22")])],"isStart":false})});
            var Q1;
            Q1=makeQuery(id+"F14.opExtrude","CAP_EDGE",EDGE,{"disambiguationData":[OSD([sQuery(id+"F8.wireOp",EDGE,"E22")])],"isStart":false});
            chamfer(context, id + "F44", {"entities" : qUnion([Q0, Q1]), "width" : 0.2 * mm, "tangentPropagation" : true});
        }
        {
            var Q0;
            Q0=makeQuery(id+"F34.opExtrude","CAP_EDGE",EDGE,{"disambiguationData":[OSD([sQuery(id+"F33.wireOp",EDGE,"E30")])],"isStart":false});
            chamfer(context, id + "F45", {"entities" : qUnion([Q0]), "width" : 0.3 * mm, "tangentPropagation" : true});
        }
    });
